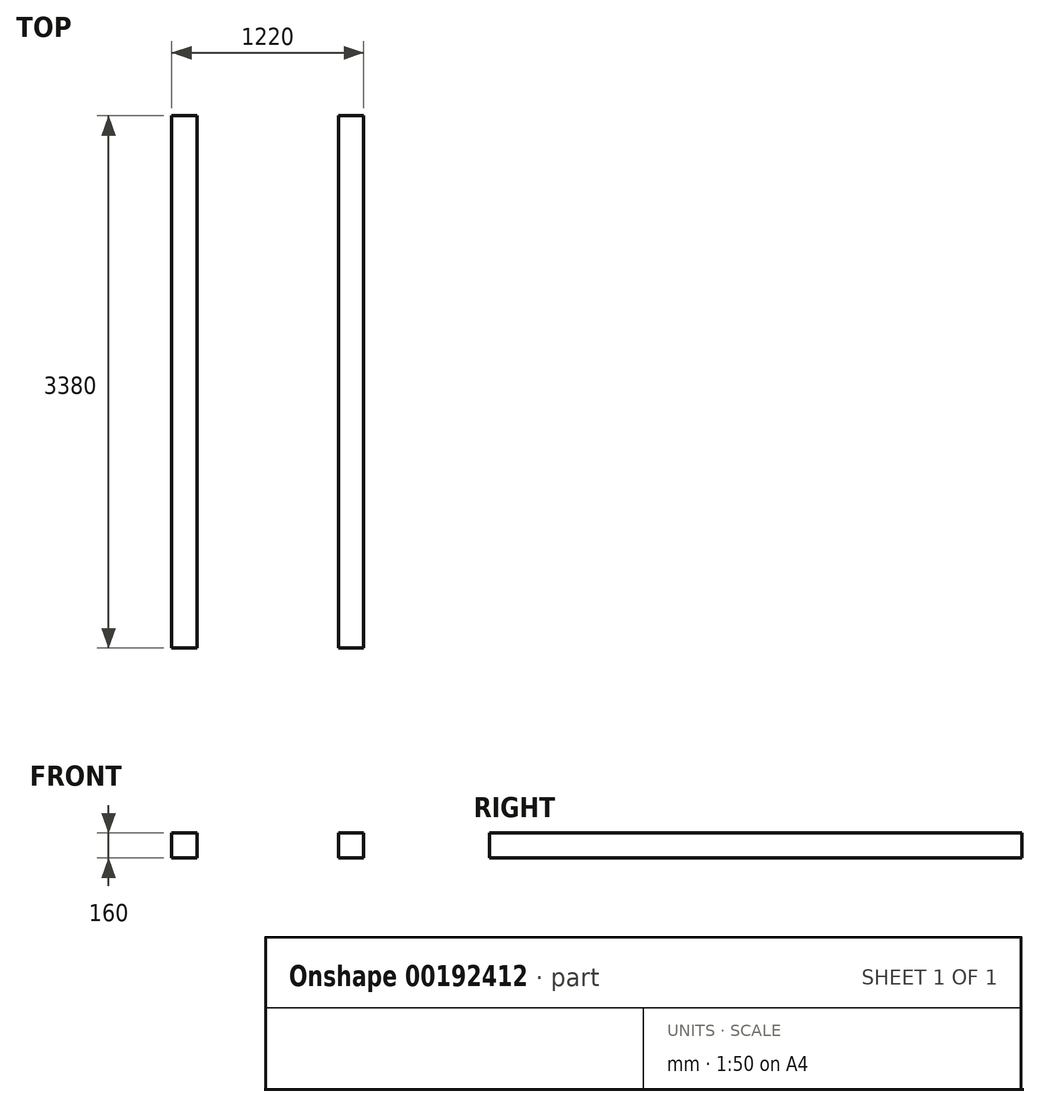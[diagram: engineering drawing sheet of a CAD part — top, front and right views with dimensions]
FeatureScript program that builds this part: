
annotation { "Feature Type Name" : "Feature", "Feature Type Description" : "" }
export const myFeature = defineFeature(function(context is Context, id is Id, definition is map)
    precondition{}
    {
        {
            var Q0;
            Q0=qCreatedBy(makeId("Top.planeOp"),FACE);
            var sketch = newSketch(context, id + "F0", { "sketchPlane" : qUnion([Q0])});
            skLineSegment(sketch, "E0.bottom", {"start": v(0, 0) * mm, "end": v(160, 0) * mm});
            skLineSegment(sketch, "E0.top", {"start": v(0, 3380) * mm, "end": v(160, 3380) * mm});
            skLineSegment(sketch, "E0.left", {"start": v(0, 0) * mm, "end": v(0, 3380) * mm});
            skLineSegment(sketch, "E0.right", {"start": v(160, 0) * mm, "end": v(160, 3380) * mm});
            skLineSegment(sketch, "E1.bottom", {"start": v(1220, 0) * mm, "end": v(1060, 0) * mm});
            skLineSegment(sketch, "E1.top", {"start": v(1220, 3380) * mm, "end": v(1060, 3380) * mm});
            skLineSegment(sketch, "E1.left", {"start": v(1220, 0) * mm, "end": v(1220, 3380) * mm});
            skLineSegment(sketch, "E1.right", {"start": v(1060, 0) * mm, "end": v(1060, 3380) * mm});
            skSolve(sketch);
        }
        {
            var Q0;
            Q0=makeQuery(id+"F0.imprint","IMPRINT",FACE,{"disambiguationData":[TD([[makeQuery(id+"F0.imprint","IMPRINT",EDGE,{"derivedFrom":sQuery(id+"F0.wireOp",EDGE,"E0.bottom")}),1.0]])]});
            var Q1;
            Q1=makeQuery(id+"F0.imprint","IMPRINT",FACE,{"disambiguationData":[TD([[makeQuery(id+"F0.imprint","IMPRINT",EDGE,{"derivedFrom":sQuery(id+"F0.wireOp",EDGE,"E1.bottom")}),-1.0]])]});
            extrude(context, id + "F1", {"entities" : qUnion([Q0, Q1]), "depth" : 160 * mm});
        }
    });
